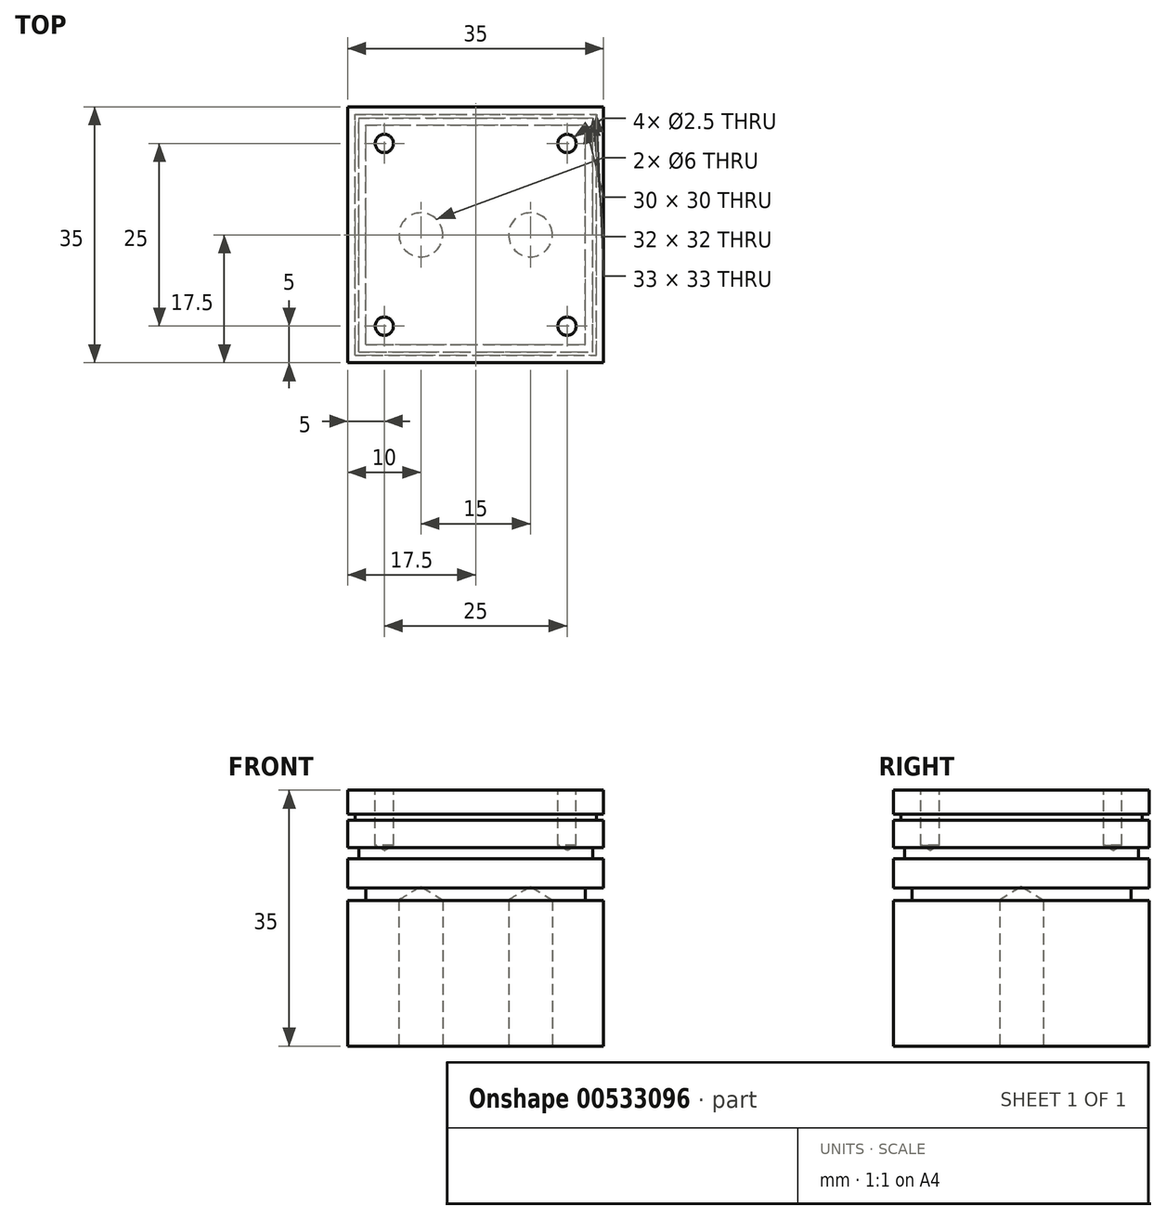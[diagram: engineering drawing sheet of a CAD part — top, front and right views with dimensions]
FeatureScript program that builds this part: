
annotation { "Feature Type Name" : "Feature", "Feature Type Description" : "" }
export const myFeature = defineFeature(function(context is Context, id is Id, definition is map)
    precondition{}
    {
        {
            var Q0;
            Q0=qCreatedBy(makeId("Front.planeOp"),FACE);
            var sketch = newSketch(context, id + "F0", { "sketchPlane" : qUnion([Q0])});
            skLineSegment(sketch, "E0", {"start": v(0, 0) * mm, "end": v(35, 0) * mm});
            skLineSegment(sketch, "E1", {"start": v(35, 35) * mm, "end": v(0, 35) * mm});
            skLineSegment(sketch, "E2", {"start": v(0, 35) * mm, "end": v(0, 31.72) * mm});
            skLineSegment(sketch, "E3", {"start": v(0, 31.72) * mm, "end": v(1, 31.72) * mm});
            skLineSegment(sketch, "E4", {"start": v(1, 31.72) * mm, "end": v(1, 30.92) * mm});
            skLineSegment(sketch, "E5", {"start": v(1, 30.92) * mm, "end": v(0, 30.92) * mm});
            skLineSegment(sketch, "E6", {"start": v(0, 30.92) * mm, "end": v(0, 27.15) * mm});
            skLineSegment(sketch, "E7", {"start": v(0, 27.15) * mm, "end": v(1.5, 27.15) * mm});
            skLineSegment(sketch, "E8", {"start": v(1.5, 27.15) * mm, "end": v(1.5, 25.65) * mm});
            skLineSegment(sketch, "E9", {"start": v(1.5, 25.65) * mm, "end": v(0, 25.65) * mm});
            skLineSegment(sketch, "E10", {"start": v(0, 25.65) * mm, "end": v(0, 21.63) * mm});
            skLineSegment(sketch, "E11", {"start": v(0, 21.63) * mm, "end": v(2.5, 21.63) * mm});
            skLineSegment(sketch, "E12", {"start": v(2.5, 21.63) * mm, "end": v(2.5, 19.93) * mm});
            skLineSegment(sketch, "E13", {"start": v(2.5, 19.93) * mm, "end": v(0, 19.93) * mm});
            skLineSegment(sketch, "E14", {"start": v(0, 19.93) * mm, "end": v(0, 0) * mm});
            skLineSegment(sketch, "E15", {"start": v(17.5, 35) * mm, "end": v(17.5, 0) * mm, "construction": true});
            skLineSegment(sketch, "E16.MirrorCS", {"start": v(34, 31.72) * mm, "end": v(34, 30.92) * mm});
            skLineSegment(sketch, "E17.MirrorCS", {"start": v(34, 30.92) * mm, "end": v(35, 30.92) * mm});
            skLineSegment(sketch, "E18.MirrorCS", {"start": v(35, 31.72) * mm, "end": v(34, 31.72) * mm});
            skLineSegment(sketch, "E19.MirrorCS", {"start": v(35, 35) * mm, "end": v(35, 31.72) * mm});
            skLineSegment(sketch, "E20.MirrorCS", {"start": v(35, 25.65) * mm, "end": v(35, 21.63) * mm});
            skLineSegment(sketch, "E21.MirrorCS", {"start": v(33.5, 27.15) * mm, "end": v(33.5, 25.65) * mm});
            skLineSegment(sketch, "E22.MirrorCS", {"start": v(35, 30.92) * mm, "end": v(35, 27.15) * mm});
            skLineSegment(sketch, "E23.MirrorCS", {"start": v(35, 19.93) * mm, "end": v(35, 0) * mm});
            skLineSegment(sketch, "E24.MirrorCS", {"start": v(32.5, 21.63) * mm, "end": v(32.5, 19.93) * mm});
            skLineSegment(sketch, "E25.MirrorCS", {"start": v(35, 21.63) * mm, "end": v(32.5, 21.63) * mm});
            skLineSegment(sketch, "E26.MirrorCS", {"start": v(32.5, 19.93) * mm, "end": v(35, 19.93) * mm});
            skLineSegment(sketch, "E27.MirrorCS", {"start": v(33.5, 25.65) * mm, "end": v(35, 25.65) * mm});
            skLineSegment(sketch, "E28.MirrorCS", {"start": v(35, 27.15) * mm, "end": v(33.5, 27.15) * mm});
            skSolve(sketch);
        }
        {
            var Q0;
            Q0=makeQuery(id+"F0.imprint","IMPRINT",FACE,{"disambiguationData":[TD([[makeQuery(id+"F0.imprint","IMPRINT",EDGE,{"derivedFrom":sQuery(id+"F0.wireOp",EDGE,"E0")}),1.0]])]});
            extrude(context, id + "F1", {"entities" : qUnion([Q0]), "depth" : 35 * mm, "offsetDistance" : 25 * mm});
        }
        {
            var Q0;
            Q0=makeQuery(id+"F1.opExtrude","SWEPT_FACE",FACE,{"disambiguationData":[OSD([sQuery(id+"F0.wireOp",EDGE,"E0")])]});
            var sketch = newSketch(context, id + "F2", { "sketchPlane" : qUnion([Q0])});
            skPoint(sketch, "E29.centerSnap0", {"position": v(0, 17.5) * mm});
            skPoint(sketch, "E30", {"position": v(10, 17.5) * mm});
            skPoint(sketch, "E31", {"position": v(25, 17.5) * mm});
            skSolve(sketch);
        }
        {
            var Q0;
            Q0=sQuery(id+"F2.wireOp",VERTEX,"E30");
            var Q1;
            Q1=sQuery(id+"F2.wireOp",VERTEX,"E31");
            var Q2;
            Q2=makeQuery(id+"F1.opExtrude","SWEPT_BODY",BODY,{"disambiguationData":[OSD([sQuery(id+"F0.wireOp",EDGE,"E0"),sQuery(id+"F0.wireOp",EDGE,"mSsrA15k-zQHr-jv3F-3yB7-AaAR6uGcFbK4"),sQuery(id+"F0.wireOp",EDGE,"E0189O29-fUcb-qWGs-mNIL-Q2Coh2gXZMAe"),sQuery(id+"F0.wireOp",EDGE,"QDZkRBJo-va1E-1S1T-eYyf-Vs8ZCXSev2yb"),sQuery(id+"F0.wireOp",EDGE,"E1"),sQuery(id+"F0.wireOp",EDGE,"E2"),sQuery(id+"F0.wireOp",EDGE,"E3"),sQuery(id+"F0.wireOp",EDGE,"E4"),sQuery(id+"F0.wireOp",EDGE,"E5"),sQuery(id+"F0.wireOp",EDGE,"E6"),sQuery(id+"F0.wireOp",EDGE,"E7"),sQuery(id+"F0.wireOp",EDGE,"E8"),sQuery(id+"F0.wireOp",EDGE,"E9"),sQuery(id+"F0.wireOp",EDGE,"E10"),sQuery(id+"F0.wireOp",EDGE,"E11"),sQuery(id+"F0.wireOp",EDGE,"E12"),sQuery(id+"F0.wireOp",EDGE,"E13"),sQuery(id+"F0.wireOp",EDGE,"E14")])]});
            hole(context, id + "F3", {"style" : HoleStyle.SIMPLE, "endStyle" : HoleEndStyle.BLIND, "holeDiameter" : 6 * mm, "holeDepth" : 20 * mm, "isTappedThrough" : true, "tappedDepth" : 12 * mm, "tapClearance" : 3, "locations" : qUnion([Q0, Q1]), "scope" : qUnion([Q2])});
        }
        {
            var Q0;
            Q0=makeQuery(id+"F1.opExtrude","SWEPT_FACE",FACE,{"disambiguationData":[OSD([sQuery(id+"F0.wireOp",EDGE,"E23.MirrorCS")])]});
            var sketch = newSketch(context, id + "F4", { "sketchPlane" : qUnion([Q0])});
            skLineSegment(sketch, "E32", {"start": v(-35, 0) * mm, "end": v(0, 0) * mm});
            skLineSegment(sketch, "E33", {"start": v(0, 35) * mm, "end": v(-35, 35) * mm});
            skLineSegment(sketch, "E34", {"start": v(-35, 35) * mm, "end": v(-35, 31.72) * mm});
            skLineSegment(sketch, "E35", {"start": v(-35, 31.72) * mm, "end": v(-34, 31.72) * mm});
            skLineSegment(sketch, "E36", {"start": v(-34, 31.72) * mm, "end": v(-34, 30.92) * mm});
            skLineSegment(sketch, "E37", {"start": v(-34, 30.92) * mm, "end": v(-35, 30.92) * mm});
            skLineSegment(sketch, "E38", {"start": v(-35, 30.92) * mm, "end": v(-35, 27.15) * mm});
            skLineSegment(sketch, "E39", {"start": v(-35, 27.15) * mm, "end": v(-33.5, 27.15) * mm});
            skLineSegment(sketch, "E40", {"start": v(-33.5, 27.15) * mm, "end": v(-33.5, 25.65) * mm});
            skLineSegment(sketch, "E41", {"start": v(-33.5, 25.65) * mm, "end": v(-35, 25.65) * mm});
            skLineSegment(sketch, "E42", {"start": v(-35, 25.65) * mm, "end": v(-35, 21.63) * mm});
            skLineSegment(sketch, "E43", {"start": v(-35, 21.63) * mm, "end": v(-32.5, 21.63) * mm});
            skLineSegment(sketch, "E44", {"start": v(-32.5, 21.63) * mm, "end": v(-32.5, 19.93) * mm});
            skLineSegment(sketch, "E45", {"start": v(-32.5, 19.93) * mm, "end": v(-35, 19.93) * mm});
            skLineSegment(sketch, "E46", {"start": v(-35, 19.93) * mm, "end": v(-35, 0) * mm});
            skLineSegment(sketch, "E47", {"start": v(-17.5, 35) * mm, "end": v(-17.5, 0) * mm, "construction": true});
            skLineSegment(sketch, "E48.MirrorCS", {"start": v(-1, 31.72) * mm, "end": v(-1, 30.92) * mm});
            skLineSegment(sketch, "E49.MirrorCS", {"start": v(-1, 30.92) * mm, "end": v(0, 30.92) * mm});
            skLineSegment(sketch, "E50.MirrorCS", {"start": v(0, 31.72) * mm, "end": v(-1, 31.72) * mm});
            skLineSegment(sketch, "E51.MirrorCS", {"start": v(0, 35) * mm, "end": v(0, 31.72) * mm});
            skLineSegment(sketch, "E52.MirrorCS", {"start": v(0, 25.65) * mm, "end": v(0, 21.63) * mm});
            skLineSegment(sketch, "E53.MirrorCS", {"start": v(-1.5, 27.15) * mm, "end": v(-1.5, 25.65) * mm});
            skLineSegment(sketch, "E54.MirrorCS", {"start": v(0, 30.92) * mm, "end": v(0, 27.15) * mm});
            skLineSegment(sketch, "E55.MirrorCS", {"start": v(0, 19.93) * mm, "end": v(0, 0) * mm});
            skLineSegment(sketch, "E56.MirrorCS", {"start": v(-2.5, 21.63) * mm, "end": v(-2.5, 19.93) * mm});
            skLineSegment(sketch, "E57.MirrorCS", {"start": v(0, 21.63) * mm, "end": v(-2.5, 21.63) * mm});
            skLineSegment(sketch, "E58.MirrorCS", {"start": v(-2.5, 19.93) * mm, "end": v(0, 19.93) * mm});
            skLineSegment(sketch, "E59.MirrorCS", {"start": v(-1.5, 25.65) * mm, "end": v(0, 25.65) * mm});
            skLineSegment(sketch, "E60.MirrorCS", {"start": v(0, 27.15) * mm, "end": v(-1.5, 27.15) * mm});
            skSolve(sketch);
        }
        {
            var Q0;
            Q0 = qSketchRegion(id + "F4", true);
            extrude(context, id + "F5", {"entities" : qUnion([Q0]), "operationType" : NewBodyOperationType.INTERSECT, "oppositeDirection" : true, "depth" : 35 * mm, "offsetDistance" : 25 * mm});
        }
        {
            var Q0;
            Q0=makeQuery(id+"F1.opExtrude","SWEPT_FACE",FACE,{"disambiguationData":[OSD([sQuery(id+"F0.wireOp",EDGE,"E1")])]});
            var sketch = newSketch(context, id + "F6", { "sketchPlane" : qUnion([Q0])});
            skPoint(sketch, "E61", {"position": v(30, -5) * mm});
            skPoint(sketch, "E62.0.1.0", {"position": v(30, -30) * mm});
            skPoint(sketch, "E62.1.0.0", {"position": v(5, -5) * mm});
            skPoint(sketch, "E62.1.1.0", {"position": v(5, -30) * mm});
            skLineSegment(sketch, "E62.direction1", {"start": v(30, -5) * mm, "end": v(5, -5) * mm, "construction": true});
            skLineSegment(sketch, "E62.direction2", {"start": v(30, -5) * mm, "end": v(30, -30) * mm, "construction": true});
            skSolve(sketch);
        }
        {
            var Q0;
            Q0=sQuery(id+"F6.wireOp",VERTEX,"E62.0.1.0");
            var Q1;
            Q1=sQuery(id+"F6.wireOp",VERTEX,"E61");
            var Q2;
            Q2=sQuery(id+"F6.wireOp",VERTEX,"E62.1.0.0");
            var Q3;
            Q3=sQuery(id+"F6.wireOp",VERTEX,"E62.1.1.0");
            var Q4;
            Q4=makeQuery(id+"F1.opExtrude","SWEPT_BODY",BODY,{"disambiguationData":[OSD([sQuery(id+"F0.wireOp",EDGE,"E0"),sQuery(id+"F0.wireOp",EDGE,"E1"),sQuery(id+"F0.wireOp",EDGE,"E2"),sQuery(id+"F0.wireOp",EDGE,"E3"),sQuery(id+"F0.wireOp",EDGE,"E4"),sQuery(id+"F0.wireOp",EDGE,"E5"),sQuery(id+"F0.wireOp",EDGE,"E6"),sQuery(id+"F0.wireOp",EDGE,"E7"),sQuery(id+"F0.wireOp",EDGE,"E8"),sQuery(id+"F0.wireOp",EDGE,"E9"),sQuery(id+"F0.wireOp",EDGE,"E10"),sQuery(id+"F0.wireOp",EDGE,"E11"),sQuery(id+"F0.wireOp",EDGE,"E12"),sQuery(id+"F0.wireOp",EDGE,"E13"),sQuery(id+"F0.wireOp",EDGE,"E14"),sQuery(id+"F0.wireOp",EDGE,"E16.MirrorCS"),sQuery(id+"F0.wireOp",EDGE,"E17.MirrorCS"),sQuery(id+"F0.wireOp",EDGE,"E18.MirrorCS"),sQuery(id+"F0.wireOp",EDGE,"E19.MirrorCS"),sQuery(id+"F0.wireOp",EDGE,"E20.MirrorCS"),sQuery(id+"F0.wireOp",EDGE,"E21.MirrorCS"),sQuery(id+"F0.wireOp",EDGE,"E22.MirrorCS"),sQuery(id+"F0.wireOp",EDGE,"E23.MirrorCS"),sQuery(id+"F0.wireOp",EDGE,"E24.MirrorCS"),sQuery(id+"F0.wireOp",EDGE,"E25.MirrorCS"),sQuery(id+"F0.wireOp",EDGE,"E26.MirrorCS"),sQuery(id+"F0.wireOp",EDGE,"E27.MirrorCS"),sQuery(id+"F0.wireOp",EDGE,"E28.MirrorCS")])]});
            hole(context, id + "F7", {"style" : HoleStyle.SIMPLE, "endStyle" : HoleEndStyle.BLIND, "standardTappedOrClearance" : lookupTablePath({ "standard" : "ISO", "engagement" : "75%", "pitch" : "0.5 mm", "size" : "M3", "type" : "Tapped" }), "standardBlindInLast" : lookupTablePath({ "standard" : "ISO", "engagement" : "75%", "pitch" : "0.5 mm", "size" : "M3", "type" : "Tapped" }), "holeDiameter" : 2.5 * mm, "showTappedDepth" : true, "holeDepth" : 7.5 * mm, "isTappedThrough" : true, "tappedDepth" : 6 * mm, "tapClearance" : 3, "locations" : qUnion([Q0, Q1, Q2, Q3]), "scope" : qUnion([Q4]), "majorDiameter" : 3 * mm});
        }
    });
